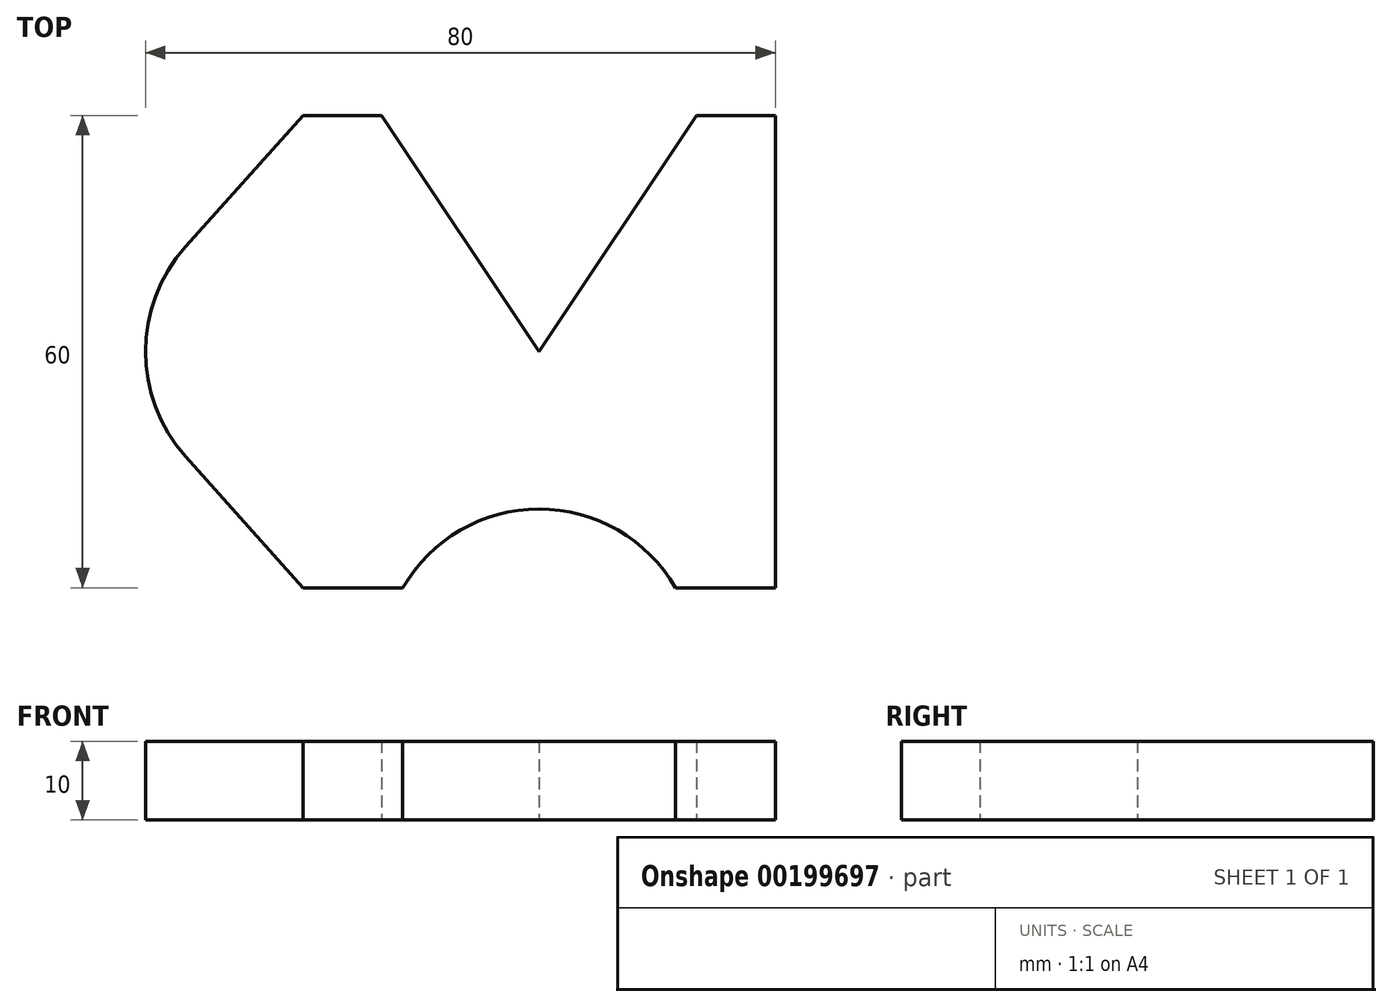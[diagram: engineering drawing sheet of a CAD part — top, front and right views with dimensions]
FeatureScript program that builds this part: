
annotation { "Feature Type Name" : "Feature", "Feature Type Description" : "" }
export const myFeature = defineFeature(function(context is Context, id is Id, definition is map)
    precondition{}
    {
        {
            var Q0;
            Q0=qCreatedBy(makeId("Top.planeOp"),FACE);
            var sketch = newSketch(context, id + "F0", { "sketchPlane" : qUnion([Q0])});
            skLineSegment(sketch, "E0", {"start": v(0, 0) * mm, "end": v(20, 30) * mm});
            skLineSegment(sketch, "E1", {"start": v(20, 30) * mm, "end": v(30, 30) * mm});
            skLineSegment(sketch, "E2", {"start": v(30, 30) * mm, "end": v(30, -30) * mm});
            skLineSegment(sketch, "E3", {"start": v(30, -30) * mm, "end": v(17.32, -30) * mm});
            skLineSegment(sketch, "E4", {"start": v(-30, 30) * mm, "end": v(-44.9, 13.33) * mm});
            skLineSegment(sketch, "E5", {"start": v(-17.32, -30) * mm, "end": v(-30, -30) * mm});
            skLineSegment(sketch, "E6", {"start": v(-30, -30) * mm, "end": v(-44.9, -13.33) * mm});
            skArc(sketch, "E7", {"start": v(-44.9, 13.33) * mm, "mid": v(-50, 0) * mm, "end": v(-44.9, -13.33) * mm});
            skArc(sketch, "E8", {"start": v(17.32, -30) * mm, "mid": v(0, -20) * mm, "end": v(-17.32, -30) * mm});
            skLineSegment(sketch, "E9", {"start": v(-30, 30) * mm, "end": v(-30, -30) * mm, "construction": true});
            skLineSegment(sketch, "E10", {"start": v(0, 0) * mm, "end": v(-20, 30) * mm});
            skLineSegment(sketch, "E11", {"start": v(-20, 30) * mm, "end": v(-30, 30) * mm});
            skSolve(sketch);
        }
        {
            var Q0;
            Q0 = qSketchRegion(id + "F0", true);
            extrude(context, id + "F1", {"entities" : qUnion([Q0]), "depth" : 10 * mm});
        }
    });
